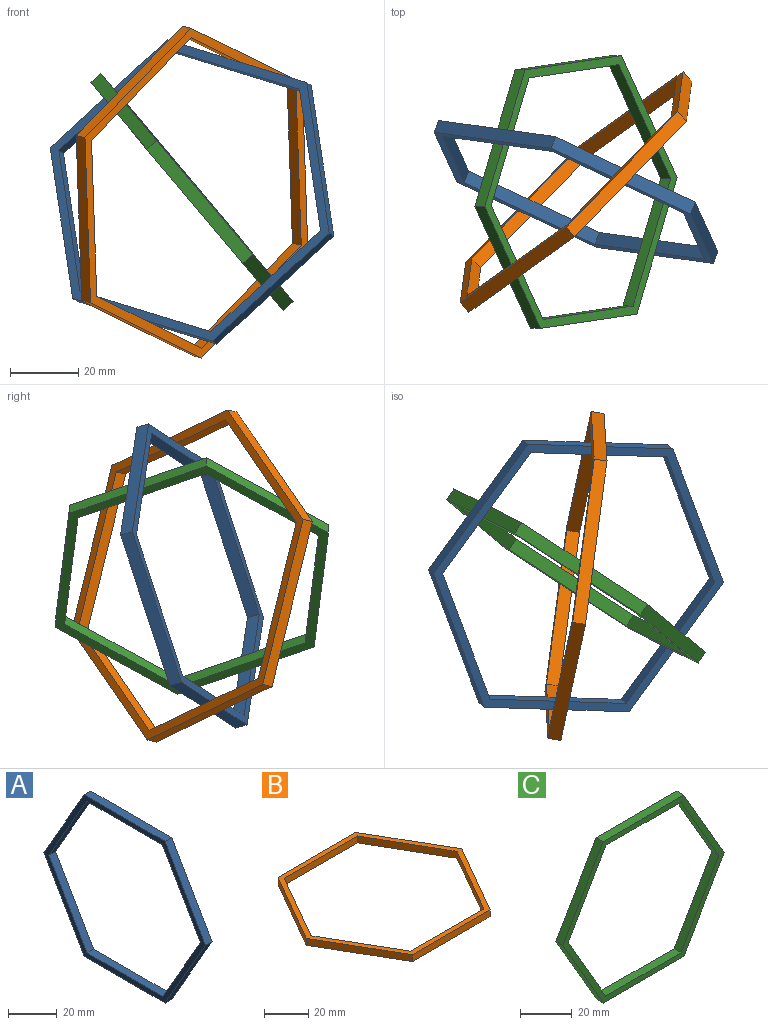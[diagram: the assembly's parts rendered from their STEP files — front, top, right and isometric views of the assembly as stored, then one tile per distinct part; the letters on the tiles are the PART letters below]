
ASSEMBLY  parts=3 mates=2
PART A: 14 faces, bbox 3.8x93.9x81.3 mm
  f0: plane 38.1x22mm, normal (0,0.87,0.5), area 167.6mm2, adj f1,f11,f12,f13
  f1: plane 38.1x22mm, normal (0,0.87,-0.5), area 167.6mm2, adj f0,f2,f12,f13
  f2: plane 43.99x3.81mm, normal (0,0,-1), area 167.6mm2, adj f1,f3,f12,f13
  f3: plane 38.1x22mm, normal (0,-0.87,-0.5), area 167.6mm2, adj f2,f4,f12,f13
  f4: plane 38.1x22mm, normal (0,-0.87,0.5), area 167.6mm2, adj f3,f11,f12,f13
  f5: plane 40.64x23.46mm, normal (0,0.87,-0.5), area 178.8mm2, adj f6,f10,f12,f13
  f6: plane 40.64x23.46mm, normal (0,0.87,0.5), area 178.8mm2, adj f5,f7,f12,f13
  f7: plane 46.93x3.81mm, normal (0,0,1), area 178.8mm2, adj f6,f8,f12,f13
  f8: plane 40.64x23.46mm, normal (0,-0.87,0.5), area 178.8mm2, adj f7,f9,f12,f13
  f9: plane 40.64x23.46mm, normal (0,-0.87,-0.5), area 178.8mm2, adj f8,f10,f12,f13
  f10: plane 46.93x3.81mm, normal (0,0,-1), area 178.8mm2, adj f5,f9,f12,f13
  f11: plane 43.99x3.81mm, normal (0,0,1), area 167.6mm2, adj f0,f4,f12,f13
  f12: plane 93.85x81.28mm, normal (1,0,0), area 692.8mm2, adj f0,f1,f2,f3,f4,f5,f6,f7
  f13: plane 93.85x81.28mm, normal (-1,0,0), area 692.8mm2, adj f0,f1,f2,f3,f4,f5,f6,f7
PART B: 14 faces, bbox 99.7x86.4x3.8 mm
  f0: plane 40.64x23.46mm, normal (0.87,0.5,0), area 178.8mm2, adj f1,f11,f12,f13
  f1: plane 40.64x23.46mm, normal (0.87,-0.5,0), area 178.8mm2, adj f0,f2,f12,f13
  f2: plane 46.93x3.81mm, normal (0,-1,0), area 178.8mm2, adj f1,f3,f12,f13
  f3: plane 40.64x23.46mm, normal (-0.87,-0.5,0), area 178.8mm2, adj f2,f4,f12,f13
  f4: plane 40.64x23.46mm, normal (-0.87,0.5,0), area 178.8mm2, adj f3,f11,f12,f13
  f5: plane 43.18x24.93mm, normal (0.87,-0.5,0), area 190mm2, adj f6,f10,f12,f13
  f6: plane 43.18x24.93mm, normal (0.87,0.5,0), area 190mm2, adj f5,f7,f12,f13
  f7: plane 49.86x3.81mm, normal (0,1,0), area 190mm2, adj f6,f8,f12,f13
  f8: plane 43.18x24.93mm, normal (-0.87,0.5,0), area 190mm2, adj f7,f9,f12,f13
  f9: plane 43.18x24.93mm, normal (-0.87,-0.5,0), area 190mm2, adj f8,f10,f12,f13
  f10: plane 49.86x3.81mm, normal (0,-1,0), area 190mm2, adj f5,f9,f12,f13
  f11: plane 46.93x3.81mm, normal (0,1,0), area 178.8mm2, adj f0,f4,f12,f13
  f12: plane 99.72x86.36mm, normal (0,0,1), area 737.5mm2, adj f0,f1,f2,f3,f4,f5,f6,f7
  f13: plane 99.72x86.36mm, normal (0,0,-1), area 737.5mm2, adj f0,f1,f2,f3,f4,f5,f6,f7
PART C: 14 faces, bbox 88x3.8x76.2 mm
  f0: plane 35.56x20.53mm, normal (0.87,0,0.5), area 156.4mm2, adj f1,f11,f12,f13
  f1: plane 35.56x20.53mm, normal (0.87,0,-0.5), area 156.4mm2, adj f0,f2,f12,f13
  f2: plane 41.06x3.81mm, normal (0,0,-1), area 156.4mm2, adj f1,f3,f12,f13
  f3: plane 35.56x20.53mm, normal (-0.87,0,-0.5), area 156.4mm2, adj f2,f4,f12,f13
  f4: plane 35.56x20.53mm, normal (-0.87,0,0.5), area 156.4mm2, adj f3,f11,f12,f13
  f5: plane 38.1x22mm, normal (0.87,0,0.5), area 167.6mm2, adj f6,f10,f12,f13
  f6: plane 43.99x3.81mm, normal (0,0,1), area 167.6mm2, adj f5,f7,f12,f13
  f7: plane 38.1x22mm, normal (-0.87,0,0.5), area 167.6mm2, adj f6,f8,f12,f13
  f8: plane 38.1x22mm, normal (-0.87,0,-0.5), area 167.6mm2, adj f7,f9,f12,f13
  f9: plane 43.99x3.81mm, normal (0,0,-1), area 167.6mm2, adj f8,f10,f12,f13
  f10: plane 38.1x22mm, normal (0.87,0,-0.5), area 167.6mm2, adj f5,f9,f12,f13
  f11: plane 41.06x3.81mm, normal (0,0,1), area 156.4mm2, adj f0,f4,f12,f13
  f12: plane 87.99x76.2mm, normal (0,-1,0), area 648.1mm2, adj f0,f1,f2,f3,f4,f5,f6,f7
  f13: plane 87.99x76.2mm, normal (0,1,0), area 648.1mm2, adj f0,f1,f2,f3,f4,f5,f6,f7
PLACE A rot(axis=(-0.46,0.49,-0.74),135.3deg) t=(-4.89,11.98,-57.02)mm
PLACE B rot(axis=(-0.66,0.22,0.72),137deg) t=(-4.89,11.98,-57.02)mm
PLACE C rot(axis=(-0.03,-0.52,0.85),111.9deg) t=(-4.89,11.98,-57.02)mm
MATE revolute A.f8 <-> B.f0  axis (0.34,0.12,0.93) through (8.96,16.81,-19.12)mm
MATE revolute C.f5 <-> A.f0  axis (-0.59,0.41,0.7) through (-27.18,27.75,-30.46)mm
